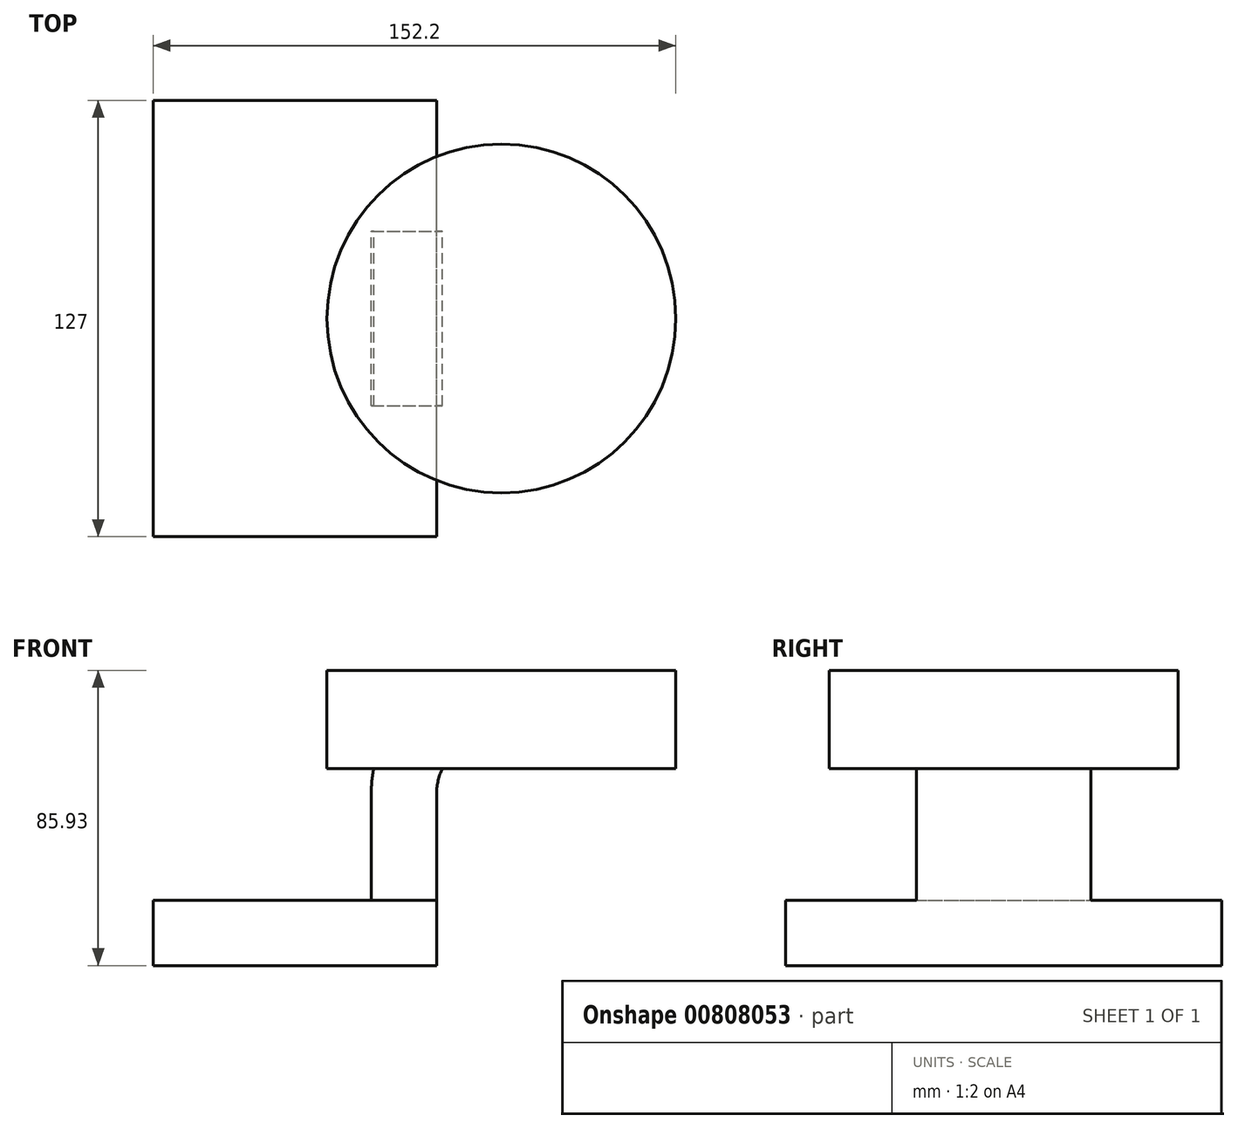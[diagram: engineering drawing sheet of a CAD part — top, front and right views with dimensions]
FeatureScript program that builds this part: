
annotation { "Feature Type Name" : "Feature", "Feature Type Description" : "" }
export const myFeature = defineFeature(function(context is Context, id is Id, definition is map)
    precondition{}
    {
        {
            var Q0;
            Q0=qCreatedBy(makeId("Front.planeOp"),FACE);
            var sketch = newSketch(context, id + "F0", { "sketchPlane" : qUnion([Q0])});
            skLineSegment(sketch, "E0.bottom", {"start": v(-41.28, 9.52) * mm, "end": v(41.27, 9.53) * mm});
            skLineSegment(sketch, "E0.top", {"start": v(-41.28, -9.53) * mm, "end": v(41.28, -9.53) * mm});
            skLineSegment(sketch, "E0.left", {"start": v(-41.28, 9.52) * mm, "end": v(-41.28, -9.53) * mm});
            skLineSegment(sketch, "E0.right", {"start": v(41.27, 9.53) * mm, "end": v(41.28, -9.52) * mm});
            skPoint(sketch, "E0.middle", {"position": v(0, 0) * mm});
            skLineSegment(sketch, "E1.bottom", {"start": v(60.13, 47.82) * mm, "end": v(110.93, 47.82) * mm});
            skLineSegment(sketch, "E1.top", {"start": v(60.13, 76.4) * mm, "end": v(110.93, 76.4) * mm});
            skLineSegment(sketch, "E1.left", {"start": v(60.13, 47.82) * mm, "end": v(60.13, 76.4) * mm});
            skLineSegment(sketch, "E1.right", {"start": v(110.93, 47.82) * mm, "end": v(110.93, 76.4) * mm});
            skPoint(sketch, "E1.middle", {"position": v(85.53, 62.1) * mm});
            skLineSegment(sketch, "E2", {"start": v(41.27, 9.53) * mm, "end": v(41.27, 40.72) * mm});
            skArc(sketch, "E3", {"start": v(41.27, 40.72) * mm, "mid": v(45.92, 51.94) * mm, "end": v(57.15, 56.6) * mm});
            skLineSegment(sketch, "E4", {"start": v(57.15, 56.6) * mm, "end": v(85.53, 56.6) * mm});
            skPoint(sketch, "E4.endSnap0", {"position": v(85.53, 47.82) * mm});
            skLineSegment(sketch, "E5.0", {"start": v(57.15, 75.64) * mm, "end": v(85.53, 75.64) * mm});
            skArc(sketch, "E5.1", {"start": v(22.23, 40.72) * mm, "mid": v(32.45, 65.41) * mm, "end": v(57.15, 75.64) * mm});
            skLineSegment(sketch, "E5.2", {"start": v(22.23, 9.53) * mm, "end": v(22.23, 40.72) * mm});
            skFitSpline(sketch, "E6", {"points": [v(-41.28, 9.52) * mm, v(60.13, 76.4) * mm], "startDerivative": vector(101.4, 66.87) * mm, "endDerivative": vector(174.06, 18.25) * mm});
            skSolve(sketch);
        }
        {
            var Q0;
            Q0=makeQuery(id+"F0.imprint","IMPRINT",FACE,{"disambiguationData":[TD([[makeQuery(id+"F0.imprint","IMPRINT",EDGE,{"derivedFrom":sQuery(id+"F0.wireOp",EDGE,"E0.top")}),1.0]])]});
            extrude(context, id + "F1", {"entities" : qUnion([Q0]), "endBound" : BoundingType.SYMMETRIC, "depth" : 127 * mm, "offsetDistance" : 25.4 * mm});
        }
        {
            var Q0;
            {var subQ0=sQuery(id+"F0.wireOp",EDGE,"E5.1");Q0=makeQuery(id+"F0.imprint","IMPRINT",FACE,{"disambiguationData":[TD([[makeQuery(id+"F0.imprint","IMPRINT",EDGE,{"derivedFrom":subQ0}),1.0]])]});}
            var Q1;
            {var subQ1=sQuery(id+"F0.wireOp",EDGE,"E2");Q1=makeQuery(id+"F0.imprint","IMPRINT",FACE,{"disambiguationData":[TD([[makeQuery(id+"F0.imprint","IMPRINT",EDGE,{"derivedFrom":subQ1}),1.0]])]});}
            extrude(context, id + "F2", {"entities" : qUnion([Q0, Q1]), "operationType" : NewBodyOperationType.ADD, "endBound" : BoundingType.SYMMETRIC, "depth" : 50.8 * mm, "offsetDistance" : 25.4 * mm});
        }
        {
            var Q0;
            {var subQ3=sQuery(id+"F0.wireOp",EDGE,"E1.bottom");Q0=makeQuery(id+"F0.imprint","IMPRINT",FACE,{"disambiguationData":[TD([[makeQuery(id+"F0.imprint","IMPRINT",EDGE,{"derivedFrom":subQ3}),1.0]])]});}
            var Q1;
            Q1=sQuery(id+"F0.wireOp",EDGE,"E1.left");
            revolve(context, id + "F3", {"operationType" : NewBodyOperationType.ADD, "surfaceOperationType" : NewSurfaceOperationType.NEW, "entities" : qUnion([Q0]), "axis" : qUnion([Q1]), "revolveType" : RevolveType.FULL});
        }
    });
